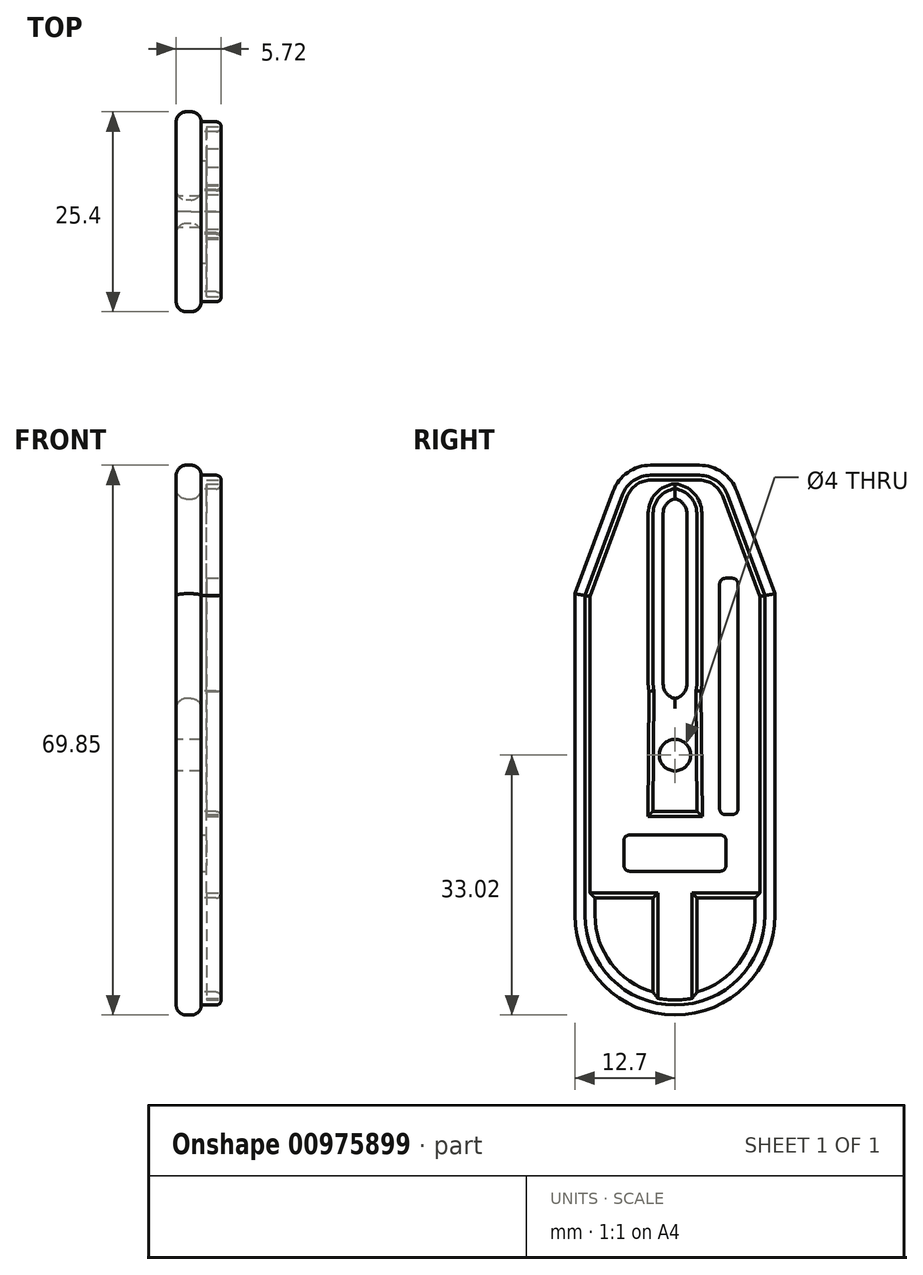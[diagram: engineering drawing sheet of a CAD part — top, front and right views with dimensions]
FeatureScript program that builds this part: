
annotation { "Feature Type Name" : "Feature", "Feature Type Description" : "" }
export const myFeature = defineFeature(function(context is Context, id is Id, definition is map)
    precondition{}
    {
        {
            var Q0;
            Q0=qCreatedBy(makeId("Right.planeOp"),FACE);
            var sketch = newSketch(context, id + "F0", { "sketchPlane" : qUnion([Q0])});
            skLineSegment(sketch, "E0", {"start": v(0, 0) * mm, "end": v(0, -40.83) * mm});
            skLineSegment(sketch, "E1", {"start": v(0, -40.83) * mm, "end": v(25.4, -40.83) * mm});
            skLineSegment(sketch, "E2", {"start": v(25.4, -40.83) * mm, "end": v(25.4, 0) * mm});
            skLineSegment(sketch, "E3", {"start": v(0, 0) * mm, "end": v(6.07, 16.32) * mm});
            skLineSegment(sketch, "E4", {"start": v(6.07, 16.32) * mm, "end": v(19.33, 16.32) * mm});
            skLineSegment(sketch, "E5", {"start": v(19.33, 16.32) * mm, "end": v(25.4, 0) * mm});
            skLineSegment(sketch, "E6.bottom", {"start": v(11.2, 12.06) * mm, "end": v(14.2, 12.06) * mm});
            skLineSegment(sketch, "E6.top", {"start": v(11.2, -13.34) * mm, "end": v(14.2, -13.34) * mm});
            skLineSegment(sketch, "E6.left", {"start": v(11.2, 12.06) * mm, "end": v(11.2, -13.34) * mm});
            skLineSegment(sketch, "E6.right", {"start": v(14.2, 12.06) * mm, "end": v(14.2, -13.34) * mm});
            skCircle(sketch, "E7", {"center": v(12.7, -20.5) * mm, "radius": 2 * mm});
            skPoint(sketch, "E7.centerSnap0", {"position": v(12.7, -13.34) * mm});
            skArc(sketch, "E8", {"start": v(0, -40.83) * mm, "mid": v(12.7, -53.53) * mm, "end": v(25.4, -40.83) * mm});
            skLineSegment(sketch, "E9", {"start": v(12.7, -53.53) * mm, "end": v(28.38, -53.53) * mm, "construction": true});
            skLineSegment(sketch, "E10", {"start": v(12.7, -20.5) * mm, "end": v(25.4, -20.5) * mm, "construction": true});
            skLineSegment(sketch, "E11", {"start": v(12.7, -20.5) * mm, "end": v(0, -20.5) * mm, "construction": true});
            skSolve(sketch);
        }
        {
            var Q0;
            Q0=makeQuery(id+"F0.imprint","IMPRINT",FACE,{"disambiguationData":[TD([[makeQuery(id+"F0.imprint","IMPRINT",EDGE,{"derivedFrom":sQuery(id+"F0.wireOp",EDGE,"E0")}),1.0]])]});
            extrude(context, id + "F1", {"entities" : qUnion([Q0]), "depth" : 3.17 * mm, "offsetDistance" : 25.4 * mm});
        }
        {
            var Q0;
            Q0=makeQuery(id+"F0.imprint","IMPRINT",FACE,{"disambiguationData":[TD([[makeQuery(id+"F0.imprint","IMPRINT",EDGE,{"derivedFrom":sQuery(id+"F0.wireOp",EDGE,"E1")}),-1.0]])]});
            extrude(context, id + "F2", {"entities" : qUnion([Q0]), "operationType" : NewBodyOperationType.ADD, "depth" : 3.17 * mm, "offsetDistance" : 25.4 * mm});
        }
        {
            var Q0;
            Q0=makeQuery(id+"F1.opExtrude","SWEPT_EDGE",EDGE,{"disambiguationData":[OSD([sQuery(id+"F0.wireOp",EDGE,"E3"),sQuery(id+"F0.wireOp",EDGE,"E4")])]});
            var Q1;
            Q1=makeQuery(id+"F1.opExtrude","SWEPT_EDGE",EDGE,{"disambiguationData":[OSD([sQuery(id+"F0.wireOp",EDGE,"E4"),sQuery(id+"F0.wireOp",EDGE,"E5")])]});
            fillet(context, id + "F3", {"entities" : qUnion([Q0, Q1]), "radius" : 5.08 * mm, "tangentPropagation" : true, "allowEdgeOverflow" : false});
        }
        {
            var Q0;
            Q0=makeQuery(id+"F1.opExtrude","SWEPT_EDGE",EDGE,{"disambiguationData":[OSD([sQuery(id+"F0.wireOp",EDGE,"E6.bottom"),sQuery(id+"F0.wireOp",EDGE,"E6.right")])]});
            var Q1;
            Q1=makeQuery(id+"F1.opExtrude","SWEPT_EDGE",EDGE,{"disambiguationData":[OSD([sQuery(id+"F0.wireOp",EDGE,"E6.bottom"),sQuery(id+"F0.wireOp",EDGE,"E6.left")])]});
            var Q2;
            Q2=makeQuery(id+"F1.opExtrude","SWEPT_EDGE",EDGE,{"disambiguationData":[OSD([sQuery(id+"F0.wireOp",EDGE,"E6.top"),sQuery(id+"F0.wireOp",EDGE,"E6.right")])]});
            var Q3;
            Q3=makeQuery(id+"F1.opExtrude","SWEPT_EDGE",EDGE,{"disambiguationData":[OSD([sQuery(id+"F0.wireOp",EDGE,"E6.top"),sQuery(id+"F0.wireOp",EDGE,"E6.left")])]});
            fillet(context, id + "F4", {"entities" : qUnion([Q0, Q1, Q2, Q3]), "radius" : 1.84 * mm, "tangentPropagation" : true, "allowEdgeOverflow" : false});
        }
        {
            var Q0;
            Q0=makeQuery(id+"F1.opExtrude","CAP_EDGE",EDGE,{"disambiguationData":[OSD([sQuery(id+"F0.wireOp",EDGE,"E4")])],"isStart":false});
            var Q1;
            Q1=makeQuery(id+"F2.opExtrude","CAP_EDGE",EDGE,{"disambiguationData":[OSD([sQuery(id+"F0.wireOp",EDGE,"E8")])],"isStart":false});
            var Q2;
            Q2=makeQuery(id+"F1.opExtrude","CAP_EDGE",EDGE,{"disambiguationData":[OSD([sQuery(id+"F0.wireOp",EDGE,"E4")])],"isStart":true});
            var Q3;
            Q3=makeQuery(id+"F2.opExtrude","CAP_EDGE",EDGE,{"disambiguationData":[OSD([sQuery(id+"F0.wireOp",EDGE,"E8")])],"isStart":true});
            fillet(context, id + "F5", {"entities" : qUnion([Q0, Q1, Q2, Q3]), "radius" : 1.27 * mm, "tangentPropagation" : true, "allowEdgeOverflow" : false});
        }
        {
            var Q0;
            {var subQ0=sQuery(id+"F0.wireOp",EDGE,"E1");var subQ1=sQuery(id+"F0.wireOp",EDGE,"E6.right");var subQ2=sQuery(id+"F0.wireOp",EDGE,"E6.top");Q0=makeQuery(id+"F4.opFillet","BLEND_EDGE",EDGE,{"blendedFrom":[makeQuery(id+"F1.opExtrude","SWEPT_EDGE",EDGE,{"disambiguationData":[OSD([subQ2,subQ1])]}),makeQuery(id+"F2.boolean.opBoolean","MERGE",FACE,{"derivedFrom":[makeQuery(id+"F1.opExtrude","CAP_FACE",FACE,{"disambiguationData":[OSD([sQuery(id+"F0.wireOp",EDGE,"E0"),subQ0,sQuery(id+"F0.wireOp",EDGE,"E2"),sQuery(id+"F0.wireOp",EDGE,"E3"),sQuery(id+"F0.wireOp",EDGE,"E4"),sQuery(id+"F0.wireOp",EDGE,"E5"),sQuery(id+"F0.wireOp",EDGE,"E6.bottom"),subQ2,sQuery(id+"F0.wireOp",EDGE,"E6.left"),subQ1,sQuery(id+"F0.wireOp",EDGE,"E7")])],"isStart":false}),makeQuery(id+"F2.opExtrude","CAP_FACE",FACE,{"disambiguationData":[OSD([subQ0,sQuery(id+"F0.wireOp",EDGE,"E8")])],"isStart":false})]})],"blendedInto":[makeQuery(id+"F2.boolean.opBoolean","MERGE",FACE,{"derivedFrom":[makeQuery(id+"F1.opExtrude","CAP_FACE",FACE,{"disambiguationData":[OSD([sQuery(id+"F0.wireOp",EDGE,"E0"),subQ0,sQuery(id+"F0.wireOp",EDGE,"E2"),sQuery(id+"F0.wireOp",EDGE,"E3"),sQuery(id+"F0.wireOp",EDGE,"E4"),sQuery(id+"F0.wireOp",EDGE,"E5"),sQuery(id+"F0.wireOp",EDGE,"E6.bottom"),subQ2,sQuery(id+"F0.wireOp",EDGE,"E6.left"),subQ1,sQuery(id+"F0.wireOp",EDGE,"E7")])],"isStart":false}),makeQuery(id+"F2.opExtrude","CAP_FACE",FACE,{"disambiguationData":[OSD([subQ0,sQuery(id+"F0.wireOp",EDGE,"E8")])],"isStart":false})]})]});}
            var Q1;
            {var subQ0=sQuery(id+"F0.wireOp",EDGE,"E1");var subQ1=sQuery(id+"F0.wireOp",EDGE,"E6.left");var subQ2=sQuery(id+"F0.wireOp",EDGE,"E6.top");Q1=makeQuery(id+"F4.opFillet","BLEND_EDGE",EDGE,{"blendedFrom":[makeQuery(id+"F1.opExtrude","SWEPT_EDGE",EDGE,{"disambiguationData":[OSD([subQ2,subQ1])]}),makeQuery(id+"F2.boolean.opBoolean","MERGE",FACE,{"derivedFrom":[makeQuery(id+"F1.opExtrude","CAP_FACE",FACE,{"disambiguationData":[OSD([sQuery(id+"F0.wireOp",EDGE,"E0"),subQ0,sQuery(id+"F0.wireOp",EDGE,"E2"),sQuery(id+"F0.wireOp",EDGE,"E3"),sQuery(id+"F0.wireOp",EDGE,"E4"),sQuery(id+"F0.wireOp",EDGE,"E5"),sQuery(id+"F0.wireOp",EDGE,"E6.bottom"),subQ2,subQ1,sQuery(id+"F0.wireOp",EDGE,"E6.right"),sQuery(id+"F0.wireOp",EDGE,"E7")])],"isStart":false}),makeQuery(id+"F2.opExtrude","CAP_FACE",FACE,{"disambiguationData":[OSD([subQ0,sQuery(id+"F0.wireOp",EDGE,"E8")])],"isStart":false})]})],"blendedInto":[makeQuery(id+"F2.boolean.opBoolean","MERGE",FACE,{"derivedFrom":[makeQuery(id+"F1.opExtrude","CAP_FACE",FACE,{"disambiguationData":[OSD([sQuery(id+"F0.wireOp",EDGE,"E0"),subQ0,sQuery(id+"F0.wireOp",EDGE,"E2"),sQuery(id+"F0.wireOp",EDGE,"E3"),sQuery(id+"F0.wireOp",EDGE,"E4"),sQuery(id+"F0.wireOp",EDGE,"E5"),sQuery(id+"F0.wireOp",EDGE,"E6.bottom"),subQ2,subQ1,sQuery(id+"F0.wireOp",EDGE,"E6.right"),sQuery(id+"F0.wireOp",EDGE,"E7")])],"isStart":false}),makeQuery(id+"F2.opExtrude","CAP_FACE",FACE,{"disambiguationData":[OSD([subQ0,sQuery(id+"F0.wireOp",EDGE,"E8")])],"isStart":false})]})]});}
            var Q2;
            Q2=makeQuery(id+"F1.opExtrude","CAP_EDGE",EDGE,{"disambiguationData":[OSD([sQuery(id+"F0.wireOp",EDGE,"E6.left")])],"isStart":true});
            var Q3;
            {var subQ0=sQuery(id+"F0.wireOp",EDGE,"E1");var subQ1=sQuery(id+"F0.wireOp",EDGE,"E6.left");var subQ2=sQuery(id+"F0.wireOp",EDGE,"E6.top");Q3=makeQuery(id+"F4.opFillet","BLEND_EDGE",EDGE,{"blendedFrom":[makeQuery(id+"F1.opExtrude","SWEPT_EDGE",EDGE,{"disambiguationData":[OSD([subQ2,subQ1])]}),makeQuery(id+"F2.boolean.opBoolean","MERGE",FACE,{"derivedFrom":[makeQuery(id+"F1.opExtrude","CAP_FACE",FACE,{"disambiguationData":[OSD([sQuery(id+"F0.wireOp",EDGE,"E0"),subQ0,sQuery(id+"F0.wireOp",EDGE,"E2"),sQuery(id+"F0.wireOp",EDGE,"E3"),sQuery(id+"F0.wireOp",EDGE,"E4"),sQuery(id+"F0.wireOp",EDGE,"E5"),sQuery(id+"F0.wireOp",EDGE,"E6.bottom"),subQ2,subQ1,sQuery(id+"F0.wireOp",EDGE,"E6.right"),sQuery(id+"F0.wireOp",EDGE,"E7")])],"isStart":true}),makeQuery(id+"F2.opExtrude","CAP_FACE",FACE,{"disambiguationData":[OSD([subQ0,sQuery(id+"F0.wireOp",EDGE,"E8")])],"isStart":true})]})],"blendedInto":[makeQuery(id+"F2.boolean.opBoolean","MERGE",FACE,{"derivedFrom":[makeQuery(id+"F1.opExtrude","CAP_FACE",FACE,{"disambiguationData":[OSD([sQuery(id+"F0.wireOp",EDGE,"E0"),subQ0,sQuery(id+"F0.wireOp",EDGE,"E2"),sQuery(id+"F0.wireOp",EDGE,"E3"),sQuery(id+"F0.wireOp",EDGE,"E4"),sQuery(id+"F0.wireOp",EDGE,"E5"),sQuery(id+"F0.wireOp",EDGE,"E6.bottom"),subQ2,subQ1,sQuery(id+"F0.wireOp",EDGE,"E6.right"),sQuery(id+"F0.wireOp",EDGE,"E7")])],"isStart":true}),makeQuery(id+"F2.opExtrude","CAP_FACE",FACE,{"disambiguationData":[OSD([subQ0,sQuery(id+"F0.wireOp",EDGE,"E8")])],"isStart":true})]})]});}
            var Q4;
            {var subQ0=sQuery(id+"F0.wireOp",EDGE,"E1");var subQ1=sQuery(id+"F0.wireOp",EDGE,"E6.right");var subQ2=sQuery(id+"F0.wireOp",EDGE,"E6.top");Q4=makeQuery(id+"F4.opFillet","BLEND_EDGE",EDGE,{"blendedFrom":[makeQuery(id+"F1.opExtrude","SWEPT_EDGE",EDGE,{"disambiguationData":[OSD([subQ2,subQ1])]}),makeQuery(id+"F2.boolean.opBoolean","MERGE",FACE,{"derivedFrom":[makeQuery(id+"F1.opExtrude","CAP_FACE",FACE,{"disambiguationData":[OSD([sQuery(id+"F0.wireOp",EDGE,"E0"),subQ0,sQuery(id+"F0.wireOp",EDGE,"E2"),sQuery(id+"F0.wireOp",EDGE,"E3"),sQuery(id+"F0.wireOp",EDGE,"E4"),sQuery(id+"F0.wireOp",EDGE,"E5"),sQuery(id+"F0.wireOp",EDGE,"E6.bottom"),subQ2,sQuery(id+"F0.wireOp",EDGE,"E6.left"),subQ1,sQuery(id+"F0.wireOp",EDGE,"E7")])],"isStart":true}),makeQuery(id+"F2.opExtrude","CAP_FACE",FACE,{"disambiguationData":[OSD([subQ0,sQuery(id+"F0.wireOp",EDGE,"E8")])],"isStart":true})]})],"blendedInto":[makeQuery(id+"F2.boolean.opBoolean","MERGE",FACE,{"derivedFrom":[makeQuery(id+"F1.opExtrude","CAP_FACE",FACE,{"disambiguationData":[OSD([sQuery(id+"F0.wireOp",EDGE,"E0"),subQ0,sQuery(id+"F0.wireOp",EDGE,"E2"),sQuery(id+"F0.wireOp",EDGE,"E3"),sQuery(id+"F0.wireOp",EDGE,"E4"),sQuery(id+"F0.wireOp",EDGE,"E5"),sQuery(id+"F0.wireOp",EDGE,"E6.bottom"),subQ2,sQuery(id+"F0.wireOp",EDGE,"E6.left"),subQ1,sQuery(id+"F0.wireOp",EDGE,"E7")])],"isStart":true}),makeQuery(id+"F2.opExtrude","CAP_FACE",FACE,{"disambiguationData":[OSD([subQ0,sQuery(id+"F0.wireOp",EDGE,"E8")])],"isStart":true})]})]});}
            var Q5;
            Q5=makeQuery(id+"F1.opExtrude","CAP_EDGE",EDGE,{"disambiguationData":[OSD([sQuery(id+"F0.wireOp",EDGE,"E6.right")])],"isStart":true});
            fillet(context, id + "F6", {"entities" : qUnion([Q0, Q1, Q2, Q3, Q4, Q5]), "radius" : 1.27 * mm, "tangentPropagation" : true, "allowEdgeOverflow" : false});
        }
        {
            var Q0;
            {var subQ0=sQuery(id+"F0.wireOp",EDGE,"E1");Q0=makeQuery(id+"F2.boolean.opBoolean","MERGE",FACE,{"derivedFrom":[makeQuery(id+"F1.opExtrude","CAP_FACE",FACE,{"disambiguationData":[OSD([sQuery(id+"F0.wireOp",EDGE,"E0"),subQ0,sQuery(id+"F0.wireOp",EDGE,"E2"),sQuery(id+"F0.wireOp",EDGE,"E3"),sQuery(id+"F0.wireOp",EDGE,"E4"),sQuery(id+"F0.wireOp",EDGE,"E5"),sQuery(id+"F0.wireOp",EDGE,"E6.bottom"),sQuery(id+"F0.wireOp",EDGE,"E6.top"),sQuery(id+"F0.wireOp",EDGE,"E6.left"),sQuery(id+"F0.wireOp",EDGE,"E6.right"),sQuery(id+"F0.wireOp",EDGE,"E7")])],"isStart":false}),makeQuery(id+"F2.opExtrude","CAP_FACE",FACE,{"disambiguationData":[OSD([subQ0,sQuery(id+"F0.wireOp",EDGE,"E8")])],"isStart":false})]});}
            var sketch = newSketch(context, id + "F7", { "sketchPlane" : qUnion([Q0])});
            skLineSegment(sketch, "E12.0", {"start": v(22.86, -0.46) * mm, "end": v(18.18, 12.13) * mm});
            skLineSegment(sketch, "E12.1", {"start": v(22.86, -40.83) * mm, "end": v(22.86, -0.46) * mm});
            skArc(sketch, "E12.2", {"start": v(18.18, 12.13) * mm, "mid": v(17.25, 13.33) * mm, "end": v(15.8, 13.78) * mm});
            skArc(sketch, "E12.3", {"start": v(2.54, -40.83) * mm, "mid": v(12.7, -50.99) * mm, "end": v(22.86, -40.83) * mm});
            skLineSegment(sketch, "E12.4", {"start": v(15.8, 13.78) * mm, "end": v(9.6, 13.78) * mm});
            skArc(sketch, "E12.5", {"start": v(9.6, 13.78) * mm, "mid": v(8.15, 13.33) * mm, "end": v(7.22, 12.13) * mm});
            skLineSegment(sketch, "E12.6", {"start": v(7.22, 12.13) * mm, "end": v(2.54, -0.46) * mm});
            skLineSegment(sketch, "E12.7", {"start": v(2.54, -0.46) * mm, "end": v(2.54, -40.83) * mm});
            skLineSegment(sketch, "E13.bottom", {"start": v(2.54, -27.66) * mm, "end": v(22.86, -27.66) * mm});
            skLineSegment(sketch, "E13.top", {"start": v(2.54, -38.67) * mm, "end": v(22.86, -38.67) * mm});
            skLineSegment(sketch, "E13.left", {"start": v(2.54, -27.66) * mm, "end": v(2.54, -38.67) * mm});
            skLineSegment(sketch, "E13.right", {"start": v(22.86, -27.66) * mm, "end": v(22.86, -38.67) * mm});
            skLineSegment(sketch, "E14", {"start": v(10.4, 20.68) * mm, "end": v(9.88, -27.66) * mm});
            skLineSegment(sketch, "E15", {"start": v(12.7, -20.5) * mm, "end": v(12.7, -50.99) * mm, "construction": true});
            skLineSegment(sketch, "E16.MirrorCS", {"start": v(15, 20.68) * mm, "end": v(15.52, -27.66) * mm});
            skLineSegment(sketch, "E17", {"start": v(2.54, -0.46) * mm, "end": v(2.25, -27.66) * mm});
            skLineSegment(sketch, "E18", {"start": v(9.88, -27.66) * mm, "end": v(15.52, -27.66) * mm});
            skLineSegment(sketch, "E19", {"start": v(22.86, -0.46) * mm, "end": v(23.15, -27.66) * mm});
            skLineSegment(sketch, "E20", {"start": v(9.88, -38.67) * mm, "end": v(9.88, -50.6) * mm});
            skLineSegment(sketch, "E21", {"start": v(15.52, -38.67) * mm, "end": v(15.52, -50.6) * mm});
            skSolve(sketch);
        }
        {
            var Q0;
            {var subQ0=sQuery(id+"F7.wireOp",EDGE,"CffNSvqF-yRKR-SQpj-RTyX-08ctVP1XR6EA");Q0=makeQuery(id+"F7.imprint","IMPRINT",FACE,{"disambiguationData":[TD([[makeQuery(id+"F7.imprint","IMPRINT",EDGE,{"derivedFrom":subQ0}),-1.0]])]});}
            var Q1;
            {var subQ0=sQuery(id+"F7.wireOp",EDGE,"dPliOB4x-Hba5-WOCV-d6CY-ONObMFQEq9AN");Q1=makeQuery(id+"F7.imprint","IMPRINT",FACE,{"disambiguationData":[TD([[makeQuery(id+"F7.imprint","IMPRINT",EDGE,{"derivedFrom":subQ0}),1.0]])]});}
            var Q2;
            {var subQ12=sQuery(id+"F7.wireOp",EDGE,"E12.0");Q2=makeQuery(id+"F7.imprint","IMPRINT",FACE,{"disambiguationData":[TD([[makeQuery(id+"F7.imprint","IMPRINT",EDGE,{"derivedFrom":subQ12}),-1.0]])]});}
            var Q3;
            {var subQ0=sQuery(id+"F7.wireOp",EDGE,"XRLydO9e-xz2z-3hUB-Hhj4-1X3KUHKsZLNA");Q3=makeQuery(id+"F7.imprint","IMPRINT",FACE,{"disambiguationData":[TD([[makeQuery(id+"F7.imprint","IMPRINT",EDGE,{"derivedFrom":subQ0}),-1.0]])]});}
            var Q4;
            {var subQ11=sQuery(id+"F7.wireOp",EDGE,"E12.4");Q4=makeQuery(id+"F7.imprint","IMPRINT",FACE,{"disambiguationData":[TD([[makeQuery(id+"F7.imprint","IMPRINT",EDGE,{"derivedFrom":subQ11}),-1.0]])]});}
            var Q5;
            {var subQ0=sQuery(id+"F7.wireOp",EDGE,"E16.MirrorCS");var subQ1=sQuery(id+"F7.wireOp",EDGE,"E12.4");var subQ2=makeQuery(id+"F7.imprint","INTERSECT",VERTEX,{"derivedFrom":[subQ1,subQ0]});Q5=makeQuery(id+"F7.imprint","IMPRINT",FACE,{"disambiguationData":[TD([[makeQuery(id+"F7.imprint","IMPRINT",EDGE,{"disambiguationData":[TD([[subQ2,-1.0]])],"derivedFrom":subQ1}),-1.0]])]});}
            var Q6;
            {var subQ11=sQuery(id+"F7.wireOp",EDGE,"E16.MirrorCS");var subQ12=sQuery(id+"F7.wireOp",EDGE,"E12.4");var subQ13=makeQuery(id+"F7.imprint","INTERSECT",VERTEX,{"derivedFrom":[subQ12,subQ11]});Q6=makeQuery(id+"F7.imprint","IMPRINT",FACE,{"disambiguationData":[TD([[makeQuery(id+"F7.imprint","IMPRINT",EDGE,{"disambiguationData":[TD([[subQ13,-1.0]])],"derivedFrom":subQ12}),1.0]])]});}
            extrude(context, id + "F8", {"entities" : qUnion([Q0, Q1, Q2, Q3, Q4, Q5, Q6]), "operationType" : NewBodyOperationType.ADD, "depth" : 2.54 * mm, "offsetDistance" : 25.4 * mm});
        }
        {
            var Q0;
            {var subQ2=sQuery(id+"F7.wireOp",EDGE,"E14");Q0=makeQuery(id+"F7.imprint","IMPRINT",FACE,{"disambiguationData":[TD([[makeQuery(id+"F7.imprint","IMPRINT",EDGE,{"derivedFrom":subQ2}),-1.0]])]});}
            var Q1;
            {var subQ2=sQuery(id+"F7.wireOp",EDGE,"E16.MirrorCS");Q1=makeQuery(id+"F7.imprint","IMPRINT",FACE,{"disambiguationData":[TD([[makeQuery(id+"F7.imprint","IMPRINT",EDGE,{"derivedFrom":subQ2}),1.0]])]});}
            var Q2;
            Q2=makeQuery(id+"F7.imprint","IMPRINT",FACE,{"disambiguationData":[TD([[makeQuery(id+"F7.imprint","IMPRINT",EDGE,{"derivedFrom":sQuery(id+"F7.wireOp",EDGE,"E13.top")}),1.0]])]});
            var Q3;
            {var subQ0=sQuery(id+"F7.wireOp",EDGE,"E20");Q3=makeQuery(id+"F7.imprint","IMPRINT",FACE,{"disambiguationData":[TD([[makeQuery(id+"F7.imprint","IMPRINT",EDGE,{"derivedFrom":subQ0}),1.0]])]});}
            extrude(context, id + "F9", {"entities" : qUnion([Q0, Q1, Q2, Q3]), "operationType" : NewBodyOperationType.ADD, "depth" : 2.54 * mm, "offsetDistance" : 25.4 * mm});
        }
        {
            var Q0;
            {var subQ0=sQuery(id+"F7.wireOp",EDGE,"E13.right");var subQ1=sQuery(id+"F7.wireOp",EDGE,"E13.left");var subQ2=sQuery(id+"F7.wireOp",EDGE,"E12.6");var subQ3=sQuery(id+"F7.wireOp",EDGE,"E12.3");var subQ4=sQuery(id+"F7.wireOp",EDGE,"E12.0");Q0=makeQuery(id+"F9.boolean.opBoolean","MERGE",FACE,{"derivedFrom":[makeQuery(id+"F8.opExtrude","CAP_FACE",FACE,{"disambiguationData":[OSD([sQuery(id+"F0.wireOp",EDGE,"E0"),sQuery(id+"F0.wireOp",EDGE,"E1"),sQuery(id+"F0.wireOp",EDGE,"E2"),sQuery(id+"F0.wireOp",EDGE,"E3"),sQuery(id+"F0.wireOp",EDGE,"E4"),sQuery(id+"F0.wireOp",EDGE,"E5"),sQuery(id+"F0.wireOp",EDGE,"E6.bottom"),sQuery(id+"F0.wireOp",EDGE,"E6.top"),sQuery(id+"F0.wireOp",EDGE,"E6.left"),sQuery(id+"F0.wireOp",EDGE,"E6.right"),sQuery(id+"F0.wireOp",EDGE,"E7"),sQuery(id+"F0.wireOp",EDGE,"E8"),subQ4,sQuery(id+"F7.wireOp",EDGE,"E12.1"),sQuery(id+"F7.wireOp",EDGE,"E12.2"),subQ3,sQuery(id+"F7.wireOp",EDGE,"E12.4"),sQuery(id+"F7.wireOp",EDGE,"E12.5"),subQ2,sQuery(id+"F7.wireOp",EDGE,"E12.7"),subQ1,subQ0])],"isStart":false}),makeQuery(id+"F9.opExtrude","CAP_FACE",FACE,{"disambiguationData":[OSD([subQ4,subQ3,subQ2,sQuery(id+"F7.wireOp",EDGE,"E13.bottom"),sQuery(id+"F7.wireOp",EDGE,"E13.top"),subQ1,subQ0,sQuery(id+"F7.wireOp",EDGE,"E14"),sQuery(id+"F7.wireOp",EDGE,"E16.MirrorCS"),sQuery(id+"F7.wireOp",EDGE,"E17"),sQuery(id+"F7.wireOp",EDGE,"E18"),sQuery(id+"F7.wireOp",EDGE,"E19"),sQuery(id+"F7.wireOp",EDGE,"E20"),sQuery(id+"F7.wireOp",EDGE,"E21")])],"isStart":false})]});}
            fillet(context, id + "F10", {"entities" : qUnion([Q0]), "tangentPropagation" : true, "radius" : 0.64 * mm, "defaultsChanged" : false, "vertexSettings" : [], "allowEdgeOverflow" : false});
        }
        {
            var Q0;
            {var subQ0=sQuery(id+"F7.wireOp",EDGE,"E19");var subQ1=sQuery(id+"F7.wireOp",EDGE,"E17");var subQ2=sQuery(id+"F7.wireOp",EDGE,"E13.right");var subQ3=sQuery(id+"F7.wireOp",EDGE,"E13.left");var subQ4=sQuery(id+"F7.wireOp",EDGE,"E12.6");var subQ5=sQuery(id+"F7.wireOp",EDGE,"E12.5");var subQ6=sQuery(id+"F7.wireOp",EDGE,"E12.3");var subQ7=sQuery(id+"F7.wireOp",EDGE,"E12.2");var subQ8=sQuery(id+"F7.wireOp",EDGE,"E12.0");Q0=makeQuery(id+"F9.boolean.opBoolean","MERGE",FACE,{"derivedFrom":[makeQuery(id+"F8.opExtrude","CAP_FACE",FACE,{"disambiguationData":[OSD([sQuery(id+"F0.wireOp",EDGE,"E0"),sQuery(id+"F0.wireOp",EDGE,"E1"),sQuery(id+"F0.wireOp",EDGE,"E2"),sQuery(id+"F0.wireOp",EDGE,"E3"),sQuery(id+"F0.wireOp",EDGE,"E4"),sQuery(id+"F0.wireOp",EDGE,"E5"),sQuery(id+"F0.wireOp",EDGE,"E6.bottom"),sQuery(id+"F0.wireOp",EDGE,"E6.top"),sQuery(id+"F0.wireOp",EDGE,"E6.left"),sQuery(id+"F0.wireOp",EDGE,"E6.right"),sQuery(id+"F0.wireOp",EDGE,"E7"),sQuery(id+"F0.wireOp",EDGE,"E8"),subQ8,sQuery(id+"F7.wireOp",EDGE,"E12.1"),subQ7,subQ6,sQuery(id+"F7.wireOp",EDGE,"E12.4"),subQ5,subQ4,sQuery(id+"F7.wireOp",EDGE,"E12.7"),subQ3,subQ2,subQ1,subQ0])],"isStart":false}),makeQuery(id+"F9.opExtrude","CAP_FACE",FACE,{"disambiguationData":[OSD([subQ8,subQ7,subQ6,subQ5,subQ4,sQuery(id+"F7.wireOp",EDGE,"E13.top"),subQ3,subQ2,sQuery(id+"F7.wireOp",EDGE,"E14"),sQuery(id+"F7.wireOp",EDGE,"E16.MirrorCS"),subQ1,sQuery(id+"F7.wireOp",EDGE,"E18"),subQ0,sQuery(id+"F7.wireOp",EDGE,"E20"),sQuery(id+"F7.wireOp",EDGE,"E21")])],"isStart":false})]});}
            var sketch = newSketch(context, id + "F11", { "sketchPlane" : qUnion([Q0])});
            skPoint(sketch, "E22.firstSnap0", {"position": v(6.21, -38.03) * mm});
            skPoint(sketch, "E22.oppositeSnap0", {"position": v(19.19, -38.03) * mm});
            skLineSegment(sketch, "E22.bottom", {"start": v(6.94, -30.65) * mm, "end": v(18.46, -30.65) * mm});
            skLineSegment(sketch, "E22.top", {"start": v(6.94, -35.25) * mm, "end": v(18.46, -35.25) * mm});
            skLineSegment(sketch, "E22.left", {"start": v(6.21, -31.37) * mm, "end": v(6.21, -34.52) * mm});
            skLineSegment(sketch, "E22.right", {"start": v(19.19, -31.37) * mm, "end": v(19.19, -34.52) * mm});
            skPoint(sketch, "E23.visualSharp", {"position": v(6.21, -30.65) * mm});
            skArc(sketch, "E23.filletArc", {"start": v(6.94, -30.65) * mm, "mid": v(6.42, -30.86) * mm, "end": v(6.21, -31.37) * mm});
            skPoint(sketch, "E24.visualSharp", {"position": v(19.19, -30.65) * mm});
            skArc(sketch, "E24.filletArc", {"start": v(19.19, -31.37) * mm, "mid": v(18.98, -30.86) * mm, "end": v(18.46, -30.65) * mm});
            skPoint(sketch, "E25.visualSharp", {"position": v(19.19, -35.25) * mm});
            skArc(sketch, "E25.filletArc", {"start": v(18.46, -35.25) * mm, "mid": v(18.98, -35.04) * mm, "end": v(19.19, -34.52) * mm});
            skPoint(sketch, "E26.visualSharp", {"position": v(6.21, -35.25) * mm});
            skArc(sketch, "E26.filletArc", {"start": v(6.21, -34.52) * mm, "mid": v(6.42, -35.04) * mm, "end": v(6.94, -35.25) * mm});
            skLineSegment(sketch, "E27.bottom", {"start": v(5.32, 1.96) * mm, "end": v(6.21, 1.96) * mm});
            skLineSegment(sketch, "E27.top", {"start": v(5.32, -28.06) * mm, "end": v(6.21, -28.06) * mm});
            skLineSegment(sketch, "E27.left", {"start": v(4.59, 1.23) * mm, "end": v(4.59, -27.33) * mm});
            skLineSegment(sketch, "E27.right", {"start": v(6.94, 1.23) * mm, "end": v(6.94, -27.33) * mm});
            skLineSegment(sketch, "E28", {"start": v(12.66, 20.13) * mm, "end": v(12.66, -51.62) * mm, "construction": true});
            skPoint(sketch, "E29.visualSharp", {"position": v(4.59, 1.96) * mm});
            skArc(sketch, "E29.filletArc", {"start": v(5.32, 1.96) * mm, "mid": v(4.8, 1.75) * mm, "end": v(4.59, 1.23) * mm});
            skPoint(sketch, "E30.visualSharp", {"position": v(6.94, 1.96) * mm});
            skArc(sketch, "E30.filletArc", {"start": v(6.94, 1.23) * mm, "mid": v(6.73, 1.75) * mm, "end": v(6.21, 1.96) * mm});
            skPoint(sketch, "E31.visualSharp", {"position": v(4.59, -28.06) * mm});
            skArc(sketch, "E31.filletArc", {"start": v(4.59, -27.33) * mm, "mid": v(4.8, -27.85) * mm, "end": v(5.32, -28.06) * mm});
            skPoint(sketch, "E32.visualSharp", {"position": v(6.94, -28.06) * mm});
            skArc(sketch, "E32.filletArc", {"start": v(6.21, -28.06) * mm, "mid": v(6.73, -27.85) * mm, "end": v(6.94, -27.33) * mm});
            skArc(sketch, "E33.MirrorCS", {"start": v(18.37, 1.23) * mm, "mid": v(18.59, 1.75) * mm, "end": v(19.1, 1.96) * mm});
            skLineSegment(sketch, "E34.MirrorCS", {"start": v(20, 1.96) * mm, "end": v(19.1, 1.96) * mm});
            skPoint(sketch, "E35.MirrorP", {"position": v(18.37, 1.96) * mm});
            skLineSegment(sketch, "E36.MirrorCS", {"start": v(20, -28.06) * mm, "end": v(19.1, -28.06) * mm});
            skArc(sketch, "E37.MirrorCS", {"start": v(20.72, -27.33) * mm, "mid": v(20.5, -27.85) * mm, "end": v(20, -28.06) * mm});
            skArc(sketch, "E38.MirrorCS", {"start": v(19.1, -28.06) * mm, "mid": v(18.59, -27.85) * mm, "end": v(18.37, -27.33) * mm});
            skLineSegment(sketch, "E39.MirrorCS", {"start": v(18.37, 1.23) * mm, "end": v(18.37, -27.33) * mm});
            skLineSegment(sketch, "E40.MirrorCS", {"start": v(20.72, 1.23) * mm, "end": v(20.72, -27.33) * mm});
            skArc(sketch, "E41.MirrorCS", {"start": v(20, 1.96) * mm, "mid": v(20.5, 1.75) * mm, "end": v(20.72, 1.23) * mm});
            skSolve(sketch);
        }
        {
            var Q0;
            Q0=makeQuery(id+"F11.imprint","IMPRINT",FACE,{"disambiguationData":[TD([[makeQuery(id+"F11.imprint","IMPRINT",EDGE,{"derivedFrom":sQuery(id+"F11.wireOp",EDGE,"E22.bottom")}),-1.0]])]});
            extrude(context, id + "F12", {"entities" : qUnion([Q0]), "operationType" : NewBodyOperationType.REMOVE, "oppositeDirection" : true, "depth" : 2.54 * mm, "offsetDistance" : 25.4 * mm});
        }
        {
            var Q0;
            Q0=makeQuery(id+"F11.imprint","IMPRINT",FACE,{"disambiguationData":[TD([[makeQuery(id+"F11.imprint","IMPRINT",EDGE,{"derivedFrom":sQuery(id+"F11.wireOp",EDGE,"E27.bottom")}),-1.0]])]});
            var Q1;
            Q1=makeQuery(id+"F11.imprint","IMPRINT",FACE,{"disambiguationData":[TD([[makeQuery(id+"F11.imprint","IMPRINT",EDGE,{"derivedFrom":sQuery(id+"F11.wireOp",EDGE,"E37.MirrorCS")}),-1.0]])]});
            extrude(context, id + "F13", {"entities" : qUnion([Q0, Q1]), "operationType" : NewBodyOperationType.REMOVE, "oppositeDirection" : true, "depth" : 1.84 * mm, "offsetDistance" : 25.4 * mm});
        }
    });
